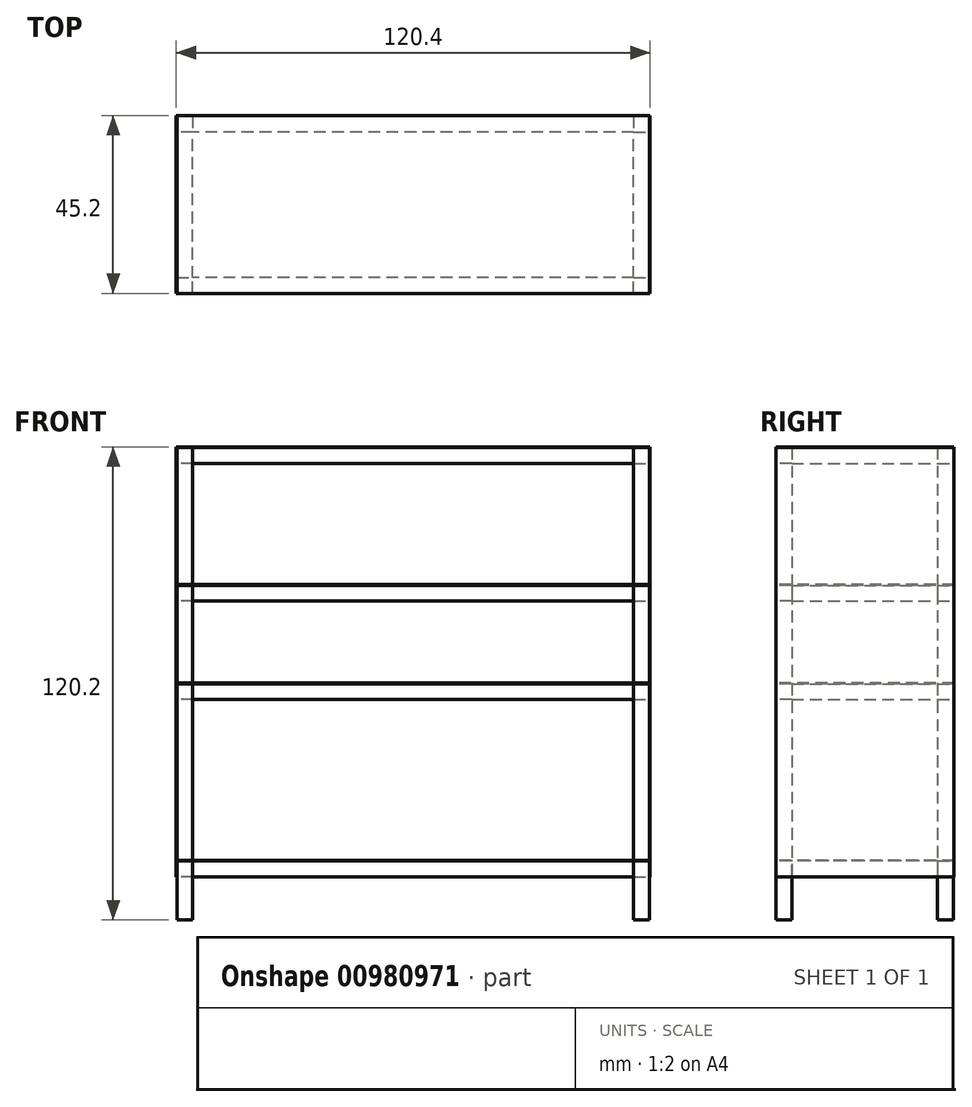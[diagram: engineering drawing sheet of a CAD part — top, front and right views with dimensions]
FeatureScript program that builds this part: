
annotation { "Feature Type Name" : "Feature", "Feature Type Description" : "" }
export const myFeature = defineFeature(function(context is Context, id is Id, definition is map)
    precondition{}
    {
        {
            var Q0;
            Q0=qCreatedBy(makeId("Top.planeOp"),FACE);
            var sketch = newSketch(context, id + "F0", { "sketchPlane" : qUnion([Q0])});
            skLineSegment(sketch, "E0.bottom", {"start": v(-60, 22.5) * mm, "end": v(-56, 22.5) * mm});
            skLineSegment(sketch, "E0.top", {"start": v(-60, 18.5) * mm, "end": v(-56, 18.5) * mm});
            skLineSegment(sketch, "E0.left", {"start": v(-60, 22.5) * mm, "end": v(-60, 18.5) * mm});
            skLineSegment(sketch, "E0.right", {"start": v(-56, 22.5) * mm, "end": v(-56, 18.5) * mm});
            skLineSegment(sketch, "E1.1.0.0", {"start": v(56, 18.5) * mm, "end": v(60, 18.5) * mm});
            skLineSegment(sketch, "E1.1.0.1", {"start": v(60, 22.5) * mm, "end": v(60, 18.5) * mm});
            skLineSegment(sketch, "E1.1.0.2", {"start": v(56, 22.5) * mm, "end": v(60, 22.5) * mm});
            skLineSegment(sketch, "E1.1.0.3", {"start": v(56, 22.5) * mm, "end": v(56, 18.5) * mm});
            skLineSegment(sketch, "E1.direction1", {"start": v(-60, 18.5) * mm, "end": v(56, 18.5) * mm, "construction": true});
            skSolve(sketch);
        }
        {
            var Q0;
            Q0 = qSketchRegion(id + "F0", true);
            extrude(context, id + "F1", {"entities" : qUnion([Q0]), "depth" : 120 * mm, "offsetDistance" : 25 * mm});
        }
        {
            var Q0;
            Q0=makeQuery(id+"F1.opExtrude","SWEPT_FACE",FACE,{"disambiguationData":[OSD([sQuery(id+"F0.wireOp",EDGE,"E0.bottom")])]});
            var sketch = newSketch(context, id + "F2", { "sketchPlane" : qUnion([Q0])});
            skLineSegment(sketch, "E2.bottom", {"start": v(-56, 120) * mm, "end": v(56, 120) * mm});
            skLineSegment(sketch, "E2.top", {"start": v(-56, 116) * mm, "end": v(56, 116) * mm});
            skLineSegment(sketch, "E2.left", {"start": v(-56, 120) * mm, "end": v(-56, 116) * mm});
            skLineSegment(sketch, "E2.right", {"start": v(56, 120) * mm, "end": v(56, 116) * mm});
            skLineSegment(sketch, "E3.0.1.0", {"start": v(-56, 81) * mm, "end": v(56, 81) * mm});
            skLineSegment(sketch, "E3.0.1.1", {"start": v(-56, 85) * mm, "end": v(-56, 81) * mm});
            skLineSegment(sketch, "E3.0.1.2", {"start": v(-56, 85) * mm, "end": v(56, 85) * mm});
            skLineSegment(sketch, "E3.0.1.3", {"start": v(56, 85) * mm, "end": v(56, 81) * mm});
            skLineSegment(sketch, "E3.direction1", {"start": v(-56, 116) * mm, "end": v(-83, 116) * mm, "construction": true});
            skLineSegment(sketch, "E3.direction2", {"start": v(-56, 116) * mm, "end": v(-56, 81) * mm, "construction": true});
            skLineSegment(sketch, "E4.0.1.0", {"start": v(-56, 56) * mm, "end": v(56, 56) * mm});
            skLineSegment(sketch, "E4.0.1.1", {"start": v(-56, 60) * mm, "end": v(56, 60) * mm});
            skLineSegment(sketch, "E4.0.1.2", {"start": v(56, 60) * mm, "end": v(56, 56) * mm});
            skLineSegment(sketch, "E4.0.1.3", {"start": v(-56, 91) * mm, "end": v(-56, 56) * mm, "construction": true});
            skLineSegment(sketch, "E4.0.1.4", {"start": v(-56, 60) * mm, "end": v(-56, 56) * mm});
            skLineSegment(sketch, "E4.direction1", {"start": v(-56, 81) * mm, "end": v(-83, 81) * mm, "construction": true});
            skLineSegment(sketch, "E4.direction2", {"start": v(-56, 81) * mm, "end": v(-56, 56) * mm, "construction": true});
            skLineSegment(sketch, "E5.0.1.0", {"start": v(-56, 11) * mm, "end": v(56, 11) * mm});
            skLineSegment(sketch, "E5.0.1.1", {"start": v(-56, 15) * mm, "end": v(56, 15) * mm});
            skLineSegment(sketch, "E5.0.1.2", {"start": v(-56, 36) * mm, "end": v(-56, 11) * mm, "construction": true});
            skLineSegment(sketch, "E5.0.1.3", {"start": v(56, 15) * mm, "end": v(56, 11) * mm});
            skLineSegment(sketch, "E5.direction1", {"start": v(-56, 56) * mm, "end": v(-33, 56) * mm, "construction": true});
            skLineSegment(sketch, "E5.direction2", {"start": v(-56, 56) * mm, "end": v(-56, 11) * mm, "construction": true});
            skLineSegment(sketch, "E6", {"start": v(-56, 15) * mm, "end": v(-56, 11) * mm});
            skSolve(sketch);
        }
        {
            var Q0;
            Q0 = qSketchRegion(id + "F2", true);
            extrude(context, id + "F3", {"entities" : qUnion([Q0]), "oppositeDirection" : true, "depth" : 4 * mm, "offsetDistance" : 25 * mm});
        }
        {
            var Q0;
            Q0=makeQuery(id+"F1.opExtrude","SWEPT_BODY",BODY,{"disambiguationData":[OSD([sQuery(id+"F0.wireOp",EDGE,"E0.bottom"),sQuery(id+"F0.wireOp",EDGE,"E0.top"),sQuery(id+"F0.wireOp",EDGE,"E0.left"),sQuery(id+"F0.wireOp",EDGE,"E0.right")])]});
            var Q1;
            Q1=makeQuery(id+"F1.opExtrude","SWEPT_BODY",BODY,{"disambiguationData":[OSD([sQuery(id+"F0.wireOp",EDGE,"E1.1.0.0"),sQuery(id+"F0.wireOp",EDGE,"E1.1.0.1"),sQuery(id+"F0.wireOp",EDGE,"E1.1.0.2"),sQuery(id+"F0.wireOp",EDGE,"E1.1.0.3")])]});
            var Q2;
            Q2=makeQuery(id+"F3.opExtrude","SWEPT_BODY",BODY,{"disambiguationData":[OSD([sQuery(id+"F2.wireOp",EDGE,"E2.bottom"),sQuery(id+"F2.wireOp",EDGE,"E2.top"),sQuery(id+"F2.wireOp",EDGE,"E2.left"),sQuery(id+"F2.wireOp",EDGE,"E2.right")])]});
            var Q3;
            Q3=makeQuery(id+"F3.opExtrude","SWEPT_BODY",BODY,{"disambiguationData":[OSD([sQuery(id+"F2.wireOp",EDGE,"E3.0.1.0"),sQuery(id+"F2.wireOp",EDGE,"E3.0.1.1"),sQuery(id+"F2.wireOp",EDGE,"E3.0.1.2"),sQuery(id+"F2.wireOp",EDGE,"E3.0.1.3")])]});
            var Q4;
            Q4=makeQuery(id+"F3.opExtrude","SWEPT_BODY",BODY,{"disambiguationData":[OSD([sQuery(id+"F2.wireOp",EDGE,"E4.0.1.0"),sQuery(id+"F2.wireOp",EDGE,"E4.0.1.1"),sQuery(id+"F2.wireOp",EDGE,"E4.0.1.2"),sQuery(id+"F2.wireOp",EDGE,"E4.0.1.4")])]});
            var Q5;
            Q5=makeQuery(id+"F3.opExtrude","SWEPT_BODY",BODY,{"disambiguationData":[OSD([sQuery(id+"F2.wireOp",EDGE,"E5.0.1.0"),sQuery(id+"F2.wireOp",EDGE,"E5.0.1.1"),sQuery(id+"F2.wireOp",EDGE,"E5.0.1.3"),sQuery(id+"F2.wireOp",EDGE,"E6")])]});
            var Q6;
            Q6=qCreatedBy(makeId("Front.planeOp"),FACE);
            mirror(context, id + "F4", {"entities" : qUnion([Q0, Q1, Q2, Q3, Q4, Q5]), "mirrorPlane" : qUnion([Q6])});
        }
        {
            var Q0;
            Q0=makeQuery(id+"F1.opExtrude","SWEPT_FACE",FACE,{"disambiguationData":[OSD([sQuery(id+"F0.wireOp",EDGE,"E1.1.0.1")])]});
            var sketch = newSketch(context, id + "F5", { "sketchPlane" : qUnion([Q0])});
            skLineSegment(sketch, "E7.bottom", {"start": v(-18.5, 120) * mm, "end": v(18.5, 120) * mm});
            skLineSegment(sketch, "E7.top", {"start": v(-18.5, 116) * mm, "end": v(18.5, 116) * mm});
            skLineSegment(sketch, "E7.left", {"start": v(-18.5, 120) * mm, "end": v(-18.5, 116) * mm});
            skLineSegment(sketch, "E7.right", {"start": v(18.5, 120) * mm, "end": v(18.5, 116) * mm});
            skLineSegment(sketch, "E8.bottom", {"start": v(-18.5, 85) * mm, "end": v(18.5, 85) * mm});
            skLineSegment(sketch, "E8.top", {"start": v(-18.5, 81) * mm, "end": v(18.5, 81) * mm});
            skLineSegment(sketch, "E8.left", {"start": v(-18.5, 85) * mm, "end": v(-18.5, 81) * mm});
            skLineSegment(sketch, "E8.right", {"start": v(18.5, 85) * mm, "end": v(18.5, 81) * mm});
            skLineSegment(sketch, "E9.bottom", {"start": v(-18.5, 60) * mm, "end": v(18.5, 60) * mm});
            skLineSegment(sketch, "E9.top", {"start": v(-18.5, 56) * mm, "end": v(18.5, 56) * mm});
            skLineSegment(sketch, "E9.left", {"start": v(-18.5, 60) * mm, "end": v(-18.5, 56) * mm});
            skLineSegment(sketch, "E9.right", {"start": v(18.5, 60) * mm, "end": v(18.5, 56) * mm});
            skLineSegment(sketch, "E10.bottom", {"start": v(18.5, 11) * mm, "end": v(-18.5, 11) * mm});
            skLineSegment(sketch, "E10.top", {"start": v(18.5, 15) * mm, "end": v(-18.5, 15) * mm});
            skLineSegment(sketch, "E10.left", {"start": v(18.5, 11) * mm, "end": v(18.5, 15) * mm});
            skLineSegment(sketch, "E10.right", {"start": v(-18.5, 11) * mm, "end": v(-18.5, 15) * mm});
            skSolve(sketch);
        }
        {
            var Q0;
            Q0 = qSketchRegion(id + "F5", true);
            extrude(context, id + "F6", {"entities" : qUnion([Q0]), "oppositeDirection" : true, "depth" : 4 * mm, "offsetDistance" : 25 * mm});
        }
        {
            var Q0;
            Q0=makeQuery(id+"F6.opExtrude","SWEPT_BODY",BODY,{"disambiguationData":[OSD([sQuery(id+"F5.wireOp",EDGE,"E10.bottom"),sQuery(id+"F5.wireOp",EDGE,"E10.top"),sQuery(id+"F5.wireOp",EDGE,"E10.left"),sQuery(id+"F5.wireOp",EDGE,"E10.right")])]});
            var Q1;
            Q1=makeQuery(id+"F6.opExtrude","SWEPT_BODY",BODY,{"disambiguationData":[OSD([sQuery(id+"F5.wireOp",EDGE,"E9.bottom"),sQuery(id+"F5.wireOp",EDGE,"E9.top"),sQuery(id+"F5.wireOp",EDGE,"E9.left"),sQuery(id+"F5.wireOp",EDGE,"E9.right")])]});
            var Q2;
            Q2=makeQuery(id+"F6.opExtrude","SWEPT_BODY",BODY,{"disambiguationData":[OSD([sQuery(id+"F5.wireOp",EDGE,"E8.bottom"),sQuery(id+"F5.wireOp",EDGE,"E8.top"),sQuery(id+"F5.wireOp",EDGE,"E8.left"),sQuery(id+"F5.wireOp",EDGE,"E8.right")])]});
            var Q3;
            Q3=makeQuery(id+"F6.opExtrude","SWEPT_BODY",BODY,{"disambiguationData":[OSD([sQuery(id+"F5.wireOp",EDGE,"E7.bottom"),sQuery(id+"F5.wireOp",EDGE,"E7.top"),sQuery(id+"F5.wireOp",EDGE,"E7.left"),sQuery(id+"F5.wireOp",EDGE,"E7.right")])]});
            var Q4;
            Q4=qCreatedBy(makeId("Right.planeOp"),FACE);
            mirror(context, id + "F7", {"entities" : qUnion([Q0, Q1, Q2, Q3]), "mirrorPlane" : qUnion([Q4])});
        }
        {
            var Q0;
            Q0=makeQuery(id+"F3.opExtrude","CAP_FACE",FACE,{"disambiguationData":[OSD([sQuery(id+"F2.wireOp",EDGE,"E2.bottom"),sQuery(id+"F2.wireOp",EDGE,"E2.top"),sQuery(id+"F2.wireOp",EDGE,"E2.left"),sQuery(id+"F2.wireOp",EDGE,"E2.right")])],"isStart":true});
            var sketch = newSketch(context, id + "F8", { "sketchPlane" : qUnion([Q0])});
            skLineSegment(sketch, "E11.bottom", {"start": v(-60, 120) * mm, "end": v(60, 120) * mm});
            skLineSegment(sketch, "E11.top", {"start": v(-60, 11) * mm, "end": v(60, 11) * mm});
            skLineSegment(sketch, "E11.left", {"start": v(-60, 120) * mm, "end": v(-60, 11) * mm});
            skLineSegment(sketch, "E11.right", {"start": v(60, 120) * mm, "end": v(60, 11) * mm});
            skSolve(sketch);
        }
        {
            var Q0;
            Q0 = qSketchRegion(id + "F8", true);
            extrude(context, id + "F9", {"entities" : qUnion([Q0]), "depth" : 0.2 * mm, "offsetDistance" : 25 * mm});
        }
        {
            var Q0;
            Q0=makeQuery(id+"F1.opExtrude","SWEPT_FACE",FACE,{"disambiguationData":[OSD([sQuery(id+"F0.wireOp",EDGE,"E0.left")])]});
            var sketch = newSketch(context, id + "F10", { "sketchPlane" : qUnion([Q0])});
            skLineSegment(sketch, "E12.bottom", {"start": v(-22.7, 120.2) * mm, "end": v(22.5, 120.2) * mm});
            skLineSegment(sketch, "E12.top", {"start": v(-22.7, 11) * mm, "end": v(22.5, 11) * mm});
            skLineSegment(sketch, "E12.left", {"start": v(-22.7, 120.2) * mm, "end": v(-22.7, 11) * mm});
            skLineSegment(sketch, "E12.right", {"start": v(22.5, 120.2) * mm, "end": v(22.5, 11) * mm});
            skSolve(sketch);
        }
        {
            var Q0;
            Q0 = qSketchRegion(id + "F10", true);
            extrude(context, id + "F11", {"entities" : qUnion([Q0]), "depth" : 0.2 * mm, "offsetDistance" : 25 * mm});
        }
        {
            var Q0;
            Q0=makeQuery(id+"F3.opExtrude","SWEPT_FACE",FACE,{"disambiguationData":[OSD([sQuery(id+"F2.wireOp",EDGE,"E2.bottom")])]});
            var sketch = newSketch(context, id + "F12", { "sketchPlane" : qUnion([Q0])});
            skLineSegment(sketch, "E13.bottom", {"start": v(-60.2, 22.7) * mm, "end": v(60.2, 22.7) * mm});
            skLineSegment(sketch, "E13.top", {"start": v(-60.2, -22.5) * mm, "end": v(60.2, -22.5) * mm});
            skLineSegment(sketch, "E13.left", {"start": v(-60.2, 22.7) * mm, "end": v(-60.2, -22.5) * mm});
            skLineSegment(sketch, "E13.right", {"start": v(60.2, 22.7) * mm, "end": v(60.2, -22.5) * mm});
            skSolve(sketch);
        }
        {
            var Q0;
            Q0 = qSketchRegion(id + "F12", true);
            extrude(context, id + "F13", {"entities" : qUnion([Q0]), "depth" : 0.2 * mm, "offsetDistance" : 25 * mm});
        }
        {
            var Q0;
            Q0=makeQuery(id+"F1.opExtrude","SWEPT_FACE",FACE,{"disambiguationData":[OSD([sQuery(id+"F0.wireOp",EDGE,"E1.1.0.1")])]});
            var sketch = newSketch(context, id + "F14", { "sketchPlane" : qUnion([Q0])});
            skLineSegment(sketch, "E14.bottom", {"start": v(-22.5, 120.2) * mm, "end": v(22.7, 120.2) * mm});
            skLineSegment(sketch, "E14.top", {"start": v(-22.5, 11) * mm, "end": v(22.7, 11) * mm});
            skLineSegment(sketch, "E14.left", {"start": v(-22.5, 120.2) * mm, "end": v(-22.5, 11) * mm});
            skLineSegment(sketch, "E14.right", {"start": v(22.7, 120.2) * mm, "end": v(22.7, 11) * mm});
            skSolve(sketch);
        }
        {
            var Q0;
            Q0 = qSketchRegion(id + "F14", true);
            extrude(context, id + "F15", {"entities" : qUnion([Q0]), "depth" : 0.2 * mm, "offsetDistance" : 25 * mm});
        }
        {
            var Q0;
            Q0=makeQuery(id+"F3.opExtrude","SWEPT_FACE",FACE,{"disambiguationData":[OSD([sQuery(id+"F2.wireOp",EDGE,"E3.0.1.2")])]});
            var sketch = newSketch(context, id + "F16", { "sketchPlane" : qUnion([Q0])});
            skLineSegment(sketch, "E15.bottom", {"start": v(-60, 22.7) * mm, "end": v(60, 22.7) * mm});
            skLineSegment(sketch, "E15.top", {"start": v(-60, -22.5) * mm, "end": v(60, -22.5) * mm});
            skLineSegment(sketch, "E15.left", {"start": v(-60, 22.7) * mm, "end": v(-60, -22.5) * mm});
            skLineSegment(sketch, "E15.right", {"start": v(60, 22.7) * mm, "end": v(60, -22.5) * mm});
            skSolve(sketch);
        }
        {
            var Q0;
            Q0 = qSketchRegion(id + "F16", true);
            extrude(context, id + "F17", {"entities" : qUnion([Q0]), "depth" : 0.2 * mm, "offsetDistance" : 25 * mm});
        }
        {
            var Q0;
            Q0=makeQuery(id+"F3.opExtrude","SWEPT_FACE",FACE,{"disambiguationData":[OSD([sQuery(id+"F2.wireOp",EDGE,"E4.0.1.1")])]});
            var sketch = newSketch(context, id + "F18", { "sketchPlane" : qUnion([Q0])});
            skLineSegment(sketch, "E16.bottom", {"start": v(-60, 22.7) * mm, "end": v(60, 22.7) * mm});
            skLineSegment(sketch, "E16.top", {"start": v(-60, -22.5) * mm, "end": v(60, -22.5) * mm});
            skLineSegment(sketch, "E16.left", {"start": v(-60, 22.7) * mm, "end": v(-60, -22.5) * mm});
            skLineSegment(sketch, "E16.right", {"start": v(60, 22.7) * mm, "end": v(60, -22.5) * mm});
            skSolve(sketch);
        }
        {
            var Q0;
            Q0 = qSketchRegion(id + "F18", true);
            extrude(context, id + "F19", {"entities" : qUnion([Q0]), "depth" : 0.2 * mm, "offsetDistance" : 25 * mm});
        }
        {
            var Q0;
            Q0=makeQuery(id+"F6.opExtrude","SWEPT_FACE",FACE,{"disambiguationData":[OSD([sQuery(id+"F5.wireOp",EDGE,"E10.top")])]});
            var sketch = newSketch(context, id + "F20", { "sketchPlane" : qUnion([Q0])});
            skLineSegment(sketch, "E17.bottom", {"start": v(-60, 22.7) * mm, "end": v(60, 22.7) * mm});
            skLineSegment(sketch, "E17.top", {"start": v(-60, -22.5) * mm, "end": v(60, -22.5) * mm});
            skLineSegment(sketch, "E17.left", {"start": v(-60, 22.7) * mm, "end": v(-60, -22.5) * mm});
            skLineSegment(sketch, "E17.right", {"start": v(60, 22.7) * mm, "end": v(60, -22.5) * mm});
            skSolve(sketch);
        }
        {
            var Q0;
            Q0 = qSketchRegion(id + "F20", true);
            extrude(context, id + "F21", {"entities" : qUnion([Q0]), "depth" : 0.2 * mm, "offsetDistance" : 25 * mm});
        }
    });
